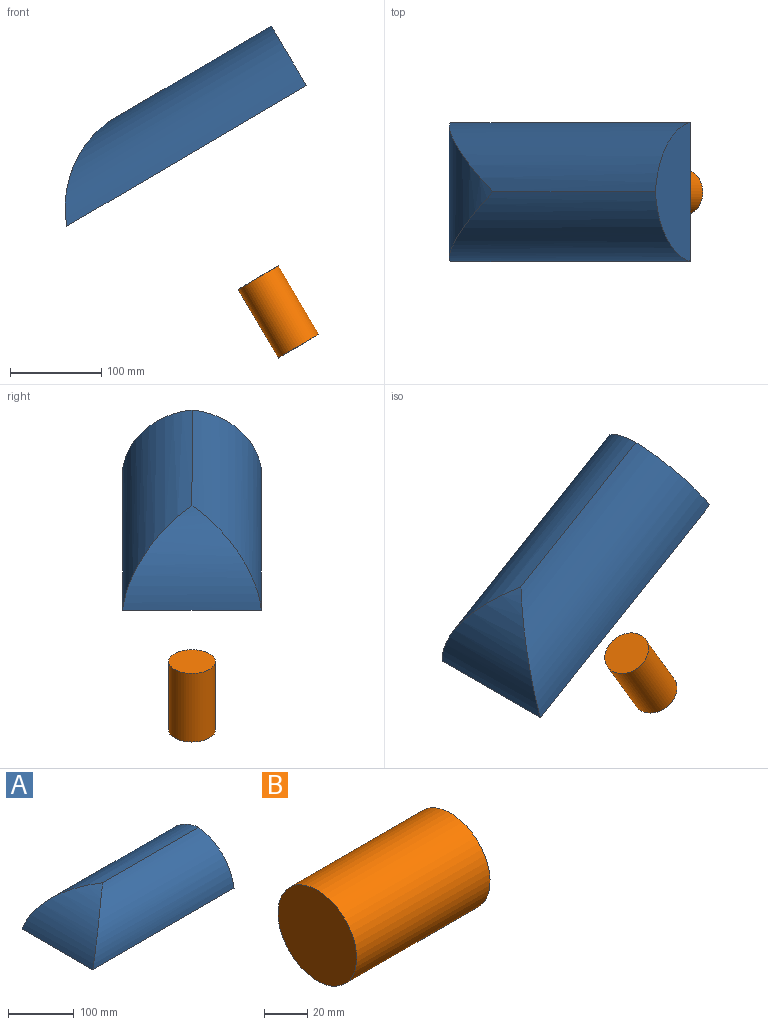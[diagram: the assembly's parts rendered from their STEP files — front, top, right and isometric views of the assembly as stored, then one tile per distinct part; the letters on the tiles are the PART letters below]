
ASSEMBLY  parts=2 mates=1
PART A: 5 faces, bbox 304.8x152.4x75.6 mm
  f0: plane 152.4x75.63mm, normal (1,0,0), area 8488.6mm2, adj f1,f3,f4
  f1: plane 304.8x152.4mm, normal (0,0,-1), area 46451.5mm2, adj f0,f2,f3,f4
  f2: cylinder r=116.41mm len=152.4mm, axis (0,-1,0), area 12049.6mm2, adj f1,f3,f4
  f3: cylinder r=86.76mm len=304.8mm, axis (-1,0,0), area 30538.2mm2, adj f0,f1,f2,f4
  f4: cylinder r=86.76mm len=304.8mm, axis (-1,0,0), area 30538.2mm2, adj f0,f1,f2,f3
PART B: 3 faces, bbox 87.3x51.4x51.4 mm
  f0: cylinder r=25.72mm len=87.29mm, axis (-1,0,0), area 14104.2mm2, adj f1,f2
  f1: plane 51.43x51.43mm, normal (1,0,0), area 2077.5mm2, adj f0
  f2: plane 51.43x51.43mm, normal (-1,0,0), area 2077.5mm2, adj f0
PLACE A rot(axis=(0,-1,0),30.5deg) t=(-315.98,-0.48,362.74)mm
PLACE B rot(axis=(0,1,0),59.5deg) t=(-211.88,24.21,199.96)mm
MATE slider B.f0 <-> A.f1  axis (-0.51,0,0.86) through (-218.09,-0.48,196.31)mm
